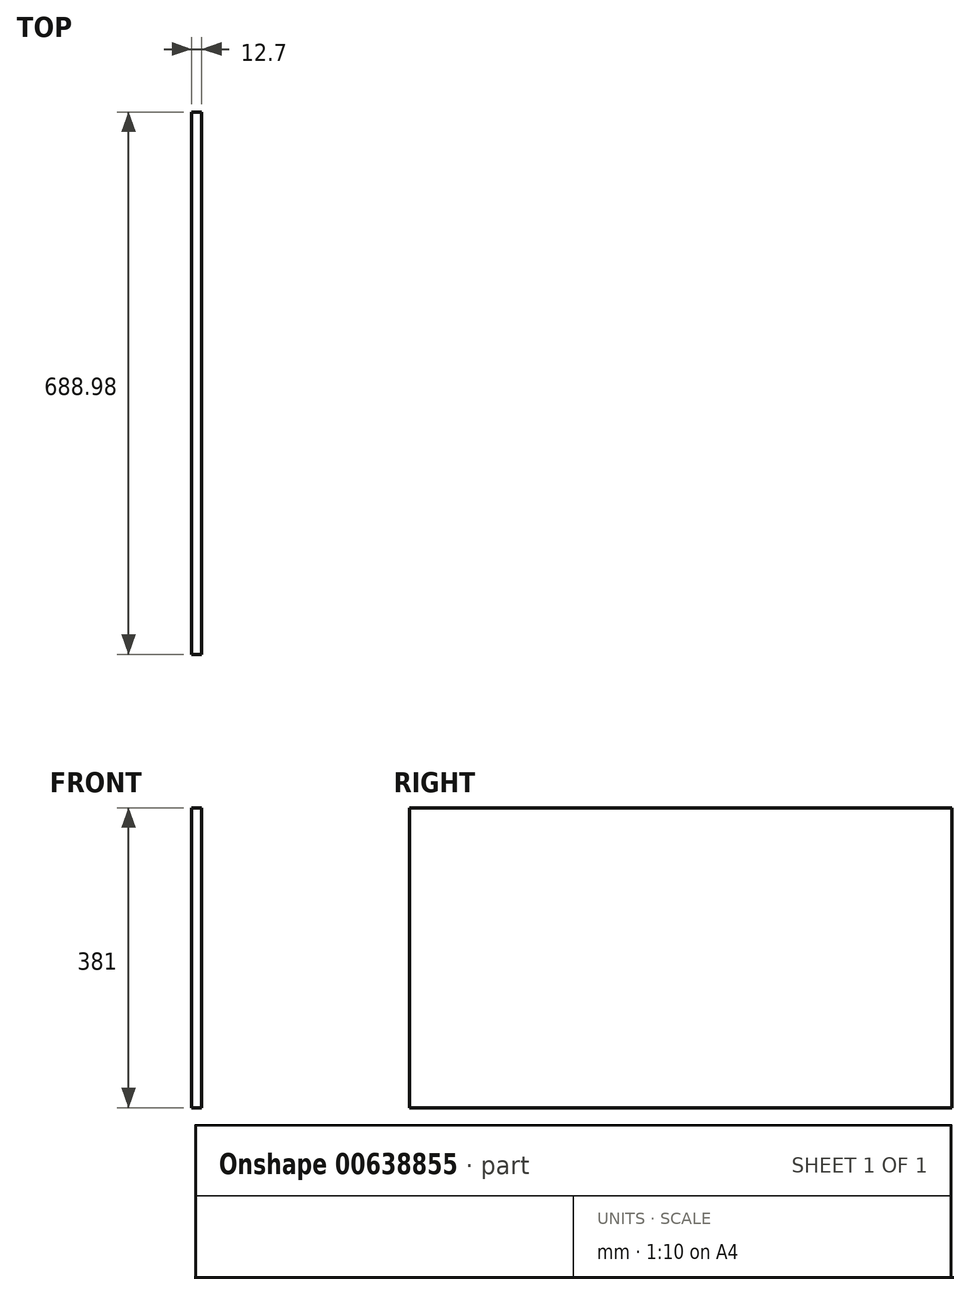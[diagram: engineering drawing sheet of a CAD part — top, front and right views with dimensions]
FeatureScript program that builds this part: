
annotation { "Feature Type Name" : "Feature", "Feature Type Description" : "" }
export const myFeature = defineFeature(function(context is Context, id is Id, definition is map)
    precondition{}
    {
        {
            var Q0;
            Q0=qCreatedBy(makeId("Right.planeOp"),FACE);
            var sketch = newSketch(context, id + "F0", { "sketchPlane" : qUnion([Q0])});
            skLineSegment(sketch, "E0.bottom", {"start": v(344.49, 190.5) * mm, "end": v(-344.49, 190.5) * mm});
            skLineSegment(sketch, "E0.top", {"start": v(344.49, -190.5) * mm, "end": v(-344.49, -190.5) * mm});
            skLineSegment(sketch, "E0.left", {"start": v(344.49, 190.5) * mm, "end": v(344.49, -190.5) * mm});
            skLineSegment(sketch, "E0.right", {"start": v(-344.49, 190.5) * mm, "end": v(-344.49, -190.5) * mm});
            skPoint(sketch, "E0.middle", {"position": v(0, 0) * mm});
            skSolve(sketch);
        }
        {
            var Q0;
            Q0=makeQuery(id+"F0.imprint","IMPRINT",FACE,{"disambiguationData":[TD([[makeQuery(id+"F0.imprint","IMPRINT",EDGE,{"derivedFrom":sQuery(id+"F0.wireOp",EDGE,"E0.bottom")}),1.0]])]});
            extrude(context, id + "F1", {"entities" : qUnion([Q0]), "depth" : 12.7 * mm, "offsetDistance" : 25.4 * mm});
        }
    });
